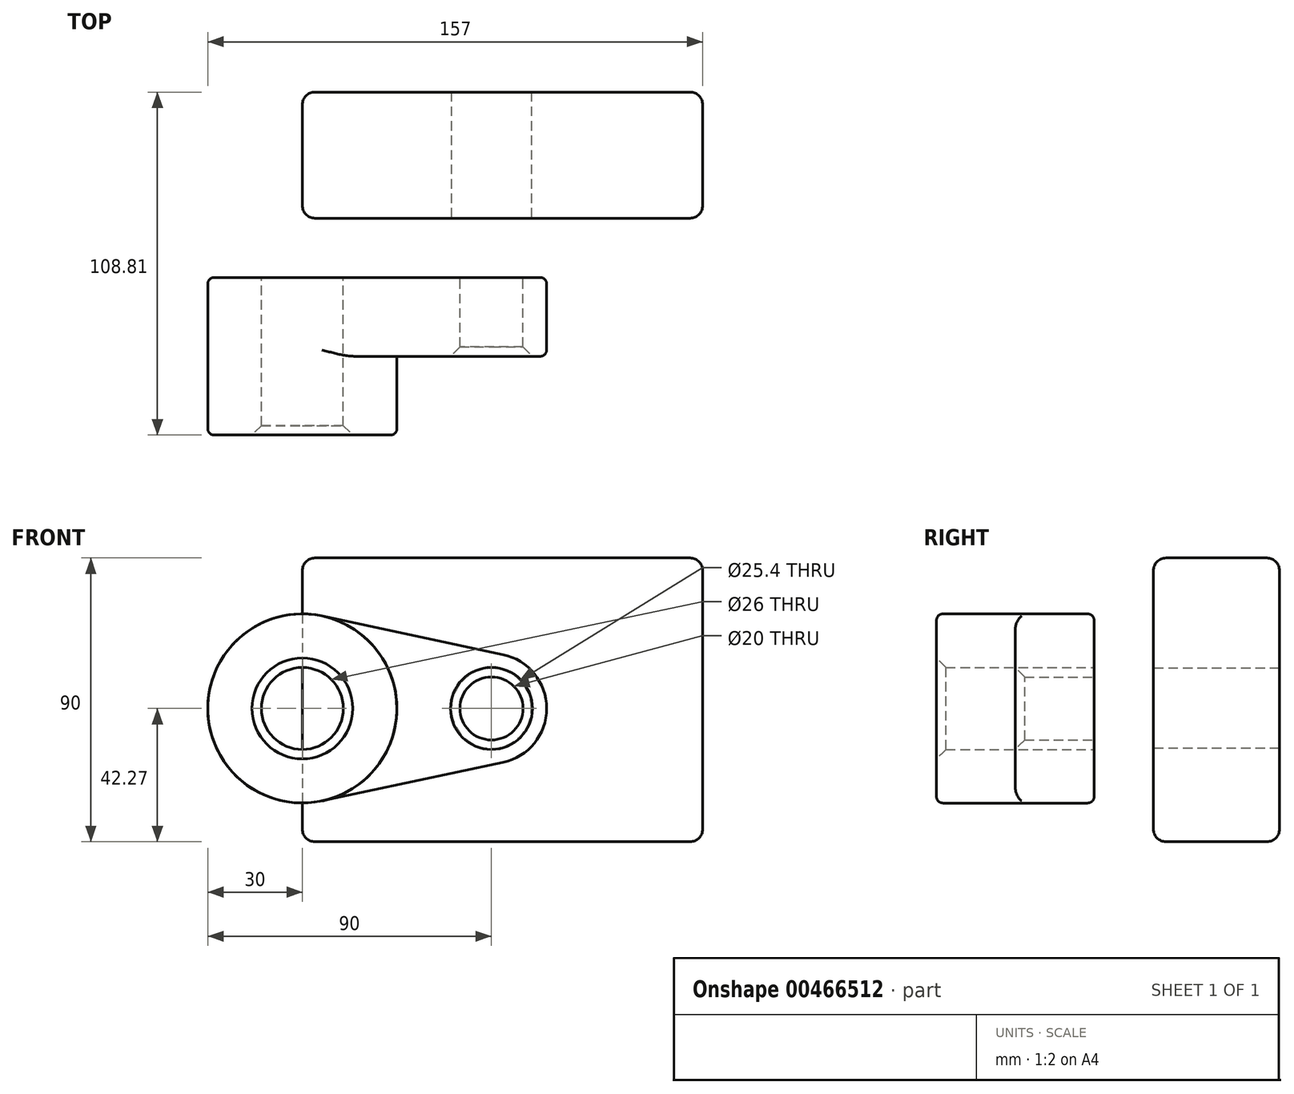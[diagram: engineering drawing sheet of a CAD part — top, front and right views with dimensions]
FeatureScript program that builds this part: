
annotation { "Feature Type Name" : "Feature", "Feature Type Description" : "" }
export const myFeature = defineFeature(function(context is Context, id is Id, definition is map)
    precondition{}
    {
        {
            var Q0;
            Q0=qCreatedBy(makeId("Front.planeOp"),FACE);
            var sketch = newSketch(context, id + "F0", { "sketchPlane" : qUnion([Q0])});
            skCircle(sketch, "E0", {"center": v(0, 0) * mm, "radius": 30 * mm});
            skCircle(sketch, "E1", {"center": v(60, 0) * mm, "radius": 17.5 * mm});
            skLineSegment(sketch, "E2", {"start": v(6.25, 29.34) * mm, "end": v(63.65, 17.12) * mm});
            skLineSegment(sketch, "E3", {"start": v(6.25, -29.34) * mm, "end": v(63.65, -17.12) * mm});
            skCircle(sketch, "E4", {"center": v(0, 0) * mm, "radius": 13 * mm});
            skCircle(sketch, "E5", {"center": v(60, 0) * mm, "radius": 10 * mm});
            skSolve(sketch);
        }
        {
            var Q0;
            Q0 = qSketchRegion(id + "F0", true);
            extrude(context, id + "F1", {"entities" : qUnion([Q0]), "depth" : 25 * mm});
        }
        {
            var Q0;
            Q0=makeQuery(id+"F0.imprint","IMPRINT",FACE,{"disambiguationData":[TD([[makeQuery(id+"F0.imprint","IMPRINT",EDGE,{"derivedFrom":sQuery(id+"F0.wireOp",EDGE,"E4")}),-1.0]])]});
            extrude(context, id + "F2", {"entities" : qUnion([Q0]), "operationType" : NewBodyOperationType.ADD, "depth" : 50 * mm});
        }
        {
            var Q0;
            Q0=makeQuery(id+"F1.opExtrude","SWEPT_FACE",FACE,{"disambiguationData":[OSD([sQuery(id+"F0.wireOp",EDGE,"E3")])]});
            var Q1;
            Q1=makeQuery(id+"F2.opExtrude","CAP_EDGE",EDGE,{"disambiguationData":[OSD([sQuery(id+"F0.wireOp",EDGE,"E0")])],"isStart":false});
            fillet(context, id + "F3", {"entities" : qUnion([Q0, Q1]), "radius" : 2 * mm, "tangentPropagation" : true, "allowEdgeOverflow" : false});
        }
        {
            var Q0;
            Q0=makeQuery(id+"F2.opExtrude","CAP_EDGE",EDGE,{"disambiguationData":[OSD([sQuery(id+"F0.wireOp",EDGE,"E4")])],"isStart":false});
            var Q1;
            Q1=makeQuery(id+"F1.opExtrude","CAP_EDGE",EDGE,{"disambiguationData":[OSD([sQuery(id+"F0.wireOp",EDGE,"E5")])],"isStart":false});
            chamfer(context, id + "F4", {"entities" : qUnion([Q0, Q1]), "width" : 3 * mm, "tangentPropagation" : true});
        }
        {
            var Q0;
            Q0=qCreatedBy(makeId("Right.planeOp"),FACE);
            var sketch = newSketch(context, id + "F5", { "sketchPlane" : qUnion([Q0])});
            skLineSegment(sketch, "E6.bottom", {"start": v(58.81, 47.73) * mm, "end": v(18.81, 47.73) * mm});
            skLineSegment(sketch, "E6.top", {"start": v(58.81, -42.27) * mm, "end": v(18.81, -42.27) * mm});
            skLineSegment(sketch, "E6.left", {"start": v(58.81, 47.73) * mm, "end": v(58.81, -42.27) * mm});
            skLineSegment(sketch, "E6.right", {"start": v(18.81, 47.73) * mm, "end": v(18.81, -42.27) * mm});
            skSolve(sketch);
        }
        {
            var Q0;
            Q0=makeQuery(id+"F5.imprint","IMPRINT",FACE,{"disambiguationData":[TD([[makeQuery(id+"F5.imprint","IMPRINT",EDGE,{"derivedFrom":sQuery(id+"F5.wireOp",EDGE,"E6.bottom")}),1.0]])]});
            extrude(context, id + "F6", {"entities" : qUnion([Q0]), "depth" : 127 * mm});
        }
        {
            var Q0;
            Q0=sQuery(id+"F0.wireOp",VERTEX,"E1.center");
            var Q1;
            Q1=makeQuery(id+"F6.opExtrude","SWEPT_BODY",BODY,{"disambiguationData":[OSD([sQuery(id+"F5.wireOp",EDGE,"E6.bottom"),sQuery(id+"F5.wireOp",EDGE,"E6.top"),sQuery(id+"F5.wireOp",EDGE,"E6.left"),sQuery(id+"F5.wireOp",EDGE,"E6.right")])]});
            hole(context, id + "F7", {"style" : HoleStyle.SIMPLE, "endStyle" : HoleEndStyle.THROUGH, "holeDiameter" : 25.4 * mm, "isTappedThrough" : true, "tappedDepth" : 12.7 * mm, "tapClearance" : 3, "locations" : qUnion([Q0]), "scope" : qUnion([Q1])});
        }
        {
            var Q0;
            Q0=makeQuery(id+"F7.hole-0.boolean.opBoolean","INTERSECT",EDGE,{"derivedFrom":[makeQuery(id+"F6.opExtrude","SWEPT_FACE",FACE,{"disambiguationData":[OSD([sQuery(id+"F5.wireOp",EDGE,"E6.left")])]}),makeQuery(id+"F7.hole-0.opRevolve","SWEPT_FACE",FACE,{"disambiguationData":[OSD([sQuery(id+"F7.hole-0.sketch.wireOp",EDGE,"core_line_2")])]})]});
            var Q1;
            Q1=makeQuery(id+"F6.opExtrude","CAP_EDGE",EDGE,{"disambiguationData":[OSD([sQuery(id+"F5.wireOp",EDGE,"E6.left")])],"isStart":false});
            var Q2;
            Q2=makeQuery(id+"F6.opExtrude","SWEPT_EDGE",EDGE,{"disambiguationData":[OSD([sQuery(id+"F5.wireOp",EDGE,"E6.top"),sQuery(id+"F5.wireOp",EDGE,"E6.left")])]});
            var Q3;
            Q3=makeQuery(id+"F6.opExtrude","SWEPT_EDGE",EDGE,{"disambiguationData":[OSD([sQuery(id+"F5.wireOp",EDGE,"E6.bottom"),sQuery(id+"F5.wireOp",EDGE,"E6.left")])]});
            var Q4;
            Q4=makeQuery(id+"F6.opExtrude","CAP_EDGE",EDGE,{"disambiguationData":[OSD([sQuery(id+"F5.wireOp",EDGE,"E6.right")])],"isStart":false});
            var Q5;
            Q5=makeQuery(id+"F6.opExtrude","CAP_EDGE",EDGE,{"disambiguationData":[OSD([sQuery(id+"F5.wireOp",EDGE,"E6.bottom")])],"isStart":false});
            var Q6;
            Q6=makeQuery(id+"F6.opExtrude","CAP_EDGE",EDGE,{"disambiguationData":[OSD([sQuery(id+"F5.wireOp",EDGE,"E6.top")])],"isStart":false});
            var Q7;
            Q7=makeQuery(id+"F6.opExtrude","SWEPT_EDGE",EDGE,{"disambiguationData":[OSD([sQuery(id+"F5.wireOp",EDGE,"E6.top"),sQuery(id+"F5.wireOp",EDGE,"E6.right")])]});
            var Q8;
            Q8=makeQuery(id+"F6.opExtrude","CAP_EDGE",EDGE,{"disambiguationData":[OSD([sQuery(id+"F5.wireOp",EDGE,"E6.top")])],"isStart":true});
            var Q9;
            Q9=makeQuery(id+"F6.opExtrude","CAP_EDGE",EDGE,{"disambiguationData":[OSD([sQuery(id+"F5.wireOp",EDGE,"E6.right")])],"isStart":true});
            var Q10;
            Q10=makeQuery(id+"F6.opExtrude","CAP_EDGE",EDGE,{"disambiguationData":[OSD([sQuery(id+"F5.wireOp",EDGE,"E6.left")])],"isStart":true});
            var Q11;
            Q11=makeQuery(id+"F6.opExtrude","CAP_EDGE",EDGE,{"disambiguationData":[OSD([sQuery(id+"F5.wireOp",EDGE,"E6.bottom")])],"isStart":true});
            var Q12;
            Q12=makeQuery(id+"F6.opExtrude","SWEPT_EDGE",EDGE,{"disambiguationData":[OSD([sQuery(id+"F5.wireOp",EDGE,"E6.bottom"),sQuery(id+"F5.wireOp",EDGE,"E6.right")])]});
            fillet(context, id + "F8", {"entities" : qUnion([Q0, Q1, Q2, Q3, Q4, Q5, Q6, Q7, Q8, Q9, Q10, Q11, Q12]), "radius" : 4 * mm, "tangentPropagation" : true, "allowEdgeOverflow" : false});
        }
    });
